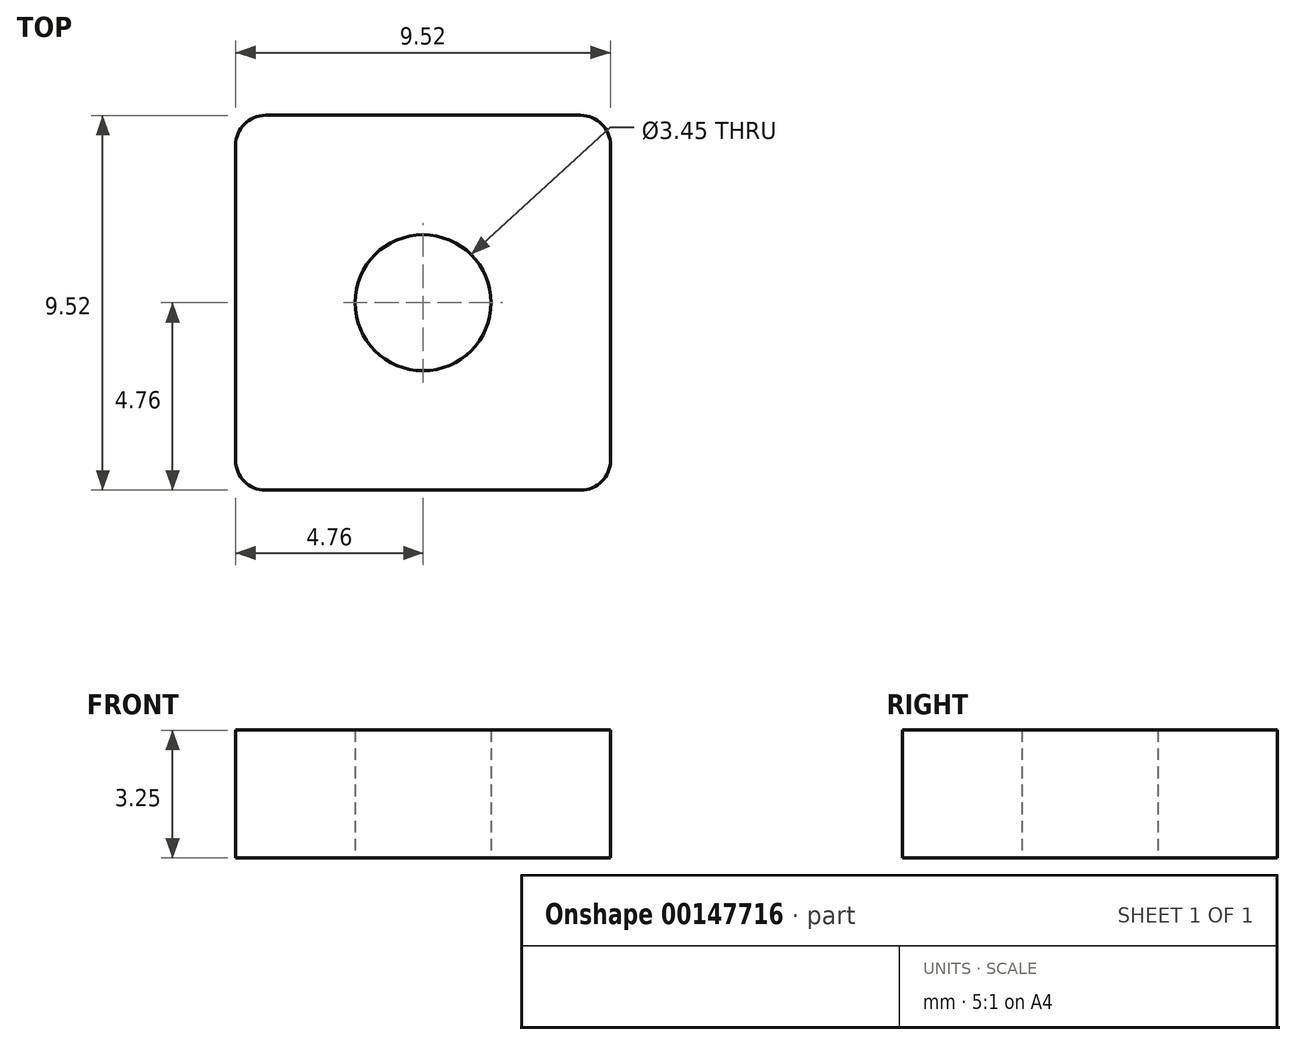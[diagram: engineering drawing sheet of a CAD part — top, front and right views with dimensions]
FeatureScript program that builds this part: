
annotation { "Feature Type Name" : "Feature", "Feature Type Description" : "" }
export const myFeature = defineFeature(function(context is Context, id is Id, definition is map)
    precondition{}
    {
        {
            var Q0;
            Q0=qCreatedBy(makeId("Top.planeOp"),FACE);
            var sketch = newSketch(context, id + "F0", { "sketchPlane" : qUnion([Q0])});
            skLineSegment(sketch, "E0.bottom", {"start": v(4.76, -4.76) * mm, "end": v(-4.76, -4.76) * mm});
            skLineSegment(sketch, "E0.top", {"start": v(4.76, 4.76) * mm, "end": v(-4.76, 4.76) * mm});
            skLineSegment(sketch, "E0.left", {"start": v(4.76, -4.76) * mm, "end": v(4.76, 4.76) * mm});
            skLineSegment(sketch, "E0.right", {"start": v(-4.76, -4.76) * mm, "end": v(-4.76, 4.76) * mm});
            skPoint(sketch, "E0.middle", {"position": v(0, 0) * mm});
            skCircle(sketch, "E1", {"center": v(0, 0) * mm, "radius": 1.73 * mm});
            skSolve(sketch);
        }
        {
            var Q0;
            Q0=qSketchRegion(id+"F0",true);
            extrude(context, id + "F1", {"entities" : qUnion([Q0]), "depth" : 3.25 * mm});
        }
        {
            var Q0;
            Q0=makeQuery(id+"F1.opExtrude","SWEPT_EDGE",EDGE,{"disambiguationData":[OSD([sQuery(id+"F0.wireOp",EDGE,"E0.top"),sQuery(id+"F0.wireOp",EDGE,"E0.right")])]});
            var Q1;
            Q1=makeQuery(id+"F1.opExtrude","SWEPT_EDGE",EDGE,{"disambiguationData":[OSD([sQuery(id+"F0.wireOp",EDGE,"E0.bottom"),sQuery(id+"F0.wireOp",EDGE,"E0.right")])]});
            var Q2;
            Q2=makeQuery(id+"F1.opExtrude","SWEPT_EDGE",EDGE,{"disambiguationData":[OSD([sQuery(id+"F0.wireOp",EDGE,"E0.top"),sQuery(id+"F0.wireOp",EDGE,"E0.left")])]});
            var Q3;
            Q3=makeQuery(id+"F1.opExtrude","SWEPT_EDGE",EDGE,{"disambiguationData":[OSD([sQuery(id+"F0.wireOp",EDGE,"E0.bottom"),sQuery(id+"F0.wireOp",EDGE,"E0.left")])]});
            fillet(context, id + "F2", {"entities" : qUnion([Q0, Q1, Q2, Q3]), "radius" : 0.76 * mm, "tangentPropagation" : true, "allowEdgeOverflow" : false});
        }
    });
